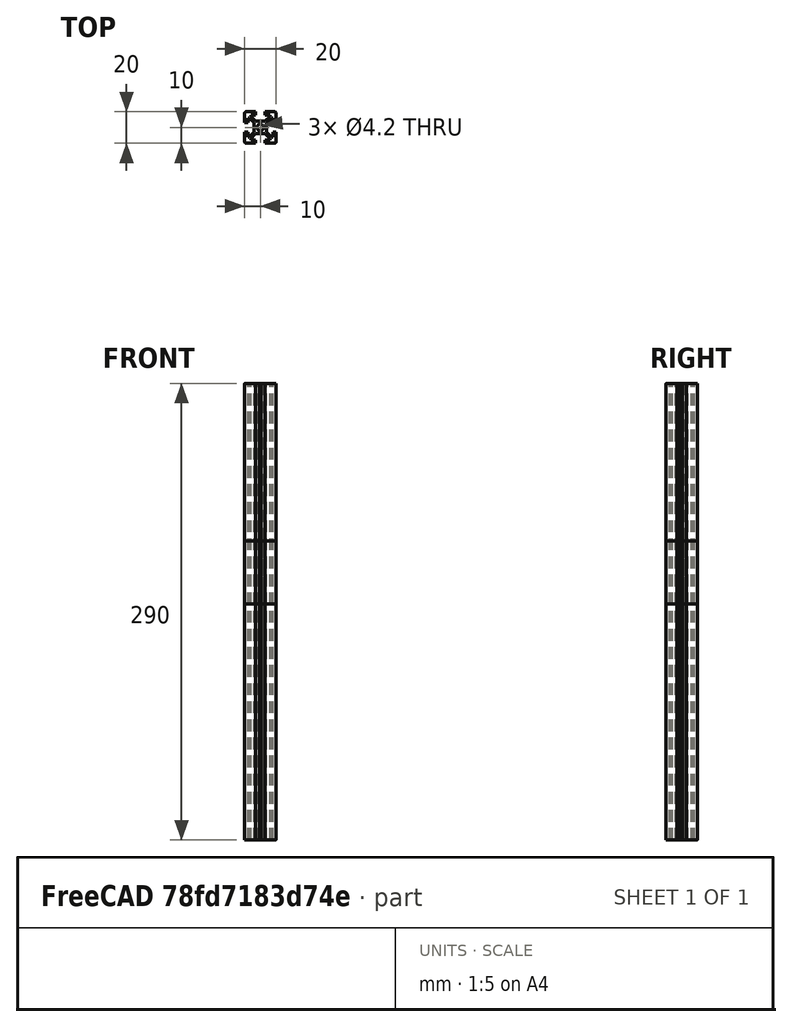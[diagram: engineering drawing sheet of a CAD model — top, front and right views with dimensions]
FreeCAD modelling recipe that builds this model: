
FCSTD DOCUMENT  (FreeCAD 0.18R16146 (Git))
Label: 2020-tslot
License: Other
LicenseURL: GPL3
objects: Part::Feature×6, Part::Extrusion×2
note: 8 computed .brp shape members not serialized (recipe doc carries the construction recipe); baked Part::Feature solids carry a one-line shape summary decoded from their .brp

FEATURE [Part::Feature] Part__Feature_cs  label="base"
  shape: bbox 20 x 20 x 2e-07 mm, 0 faces, 0 solids (baked)
FEATURE [Part::Feature] Extrude001  label="2020-290mm"
  shape: bbox 20 x 20 x 290 mm, 63 faces (baked)
FEATURE [Part::Feature] Part__Feature_cs001  label="base001"
  shape: bbox 20 x 20 x 2e-07 mm, 0 faces, 0 solids (baked)
FEATURE [Part::Extrusion] Extrude
  Base = -> Part__Feature_cs001
  Dir = (0,0,1)
  DirMode = 2
  FaceMakerClass = Part::FaceMakerBullseye
  LengthFwd = 150
  LengthRev = 0
  Solid = true
  Symmetric = false
FEATURE [Part::Feature] Extrude002  label="Extrude001"
  shape: bbox 20 x 20 x 150 mm, 63 faces (baked)
FEATURE [Part::Feature] Part__Feature_cs002  label="base002"
  shape: bbox 20 x 20 x 2e-07 mm, 0 faces, 0 solids (baked)
FEATURE [Part::Extrusion] Extrude003
  Base = -> Part__Feature_cs002
  Dir = (0,0,1)
  DirMode = 2
  FaceMakerClass = Part::FaceMakerBullseye
  LengthFwd = 190
  LengthRev = 0
  Solid = true
  Symmetric = false
FEATURE [Part::Feature] Extrude003001  label="Extrude004"
  shape: bbox 20 x 20 x 190 mm, 63 faces (baked)
